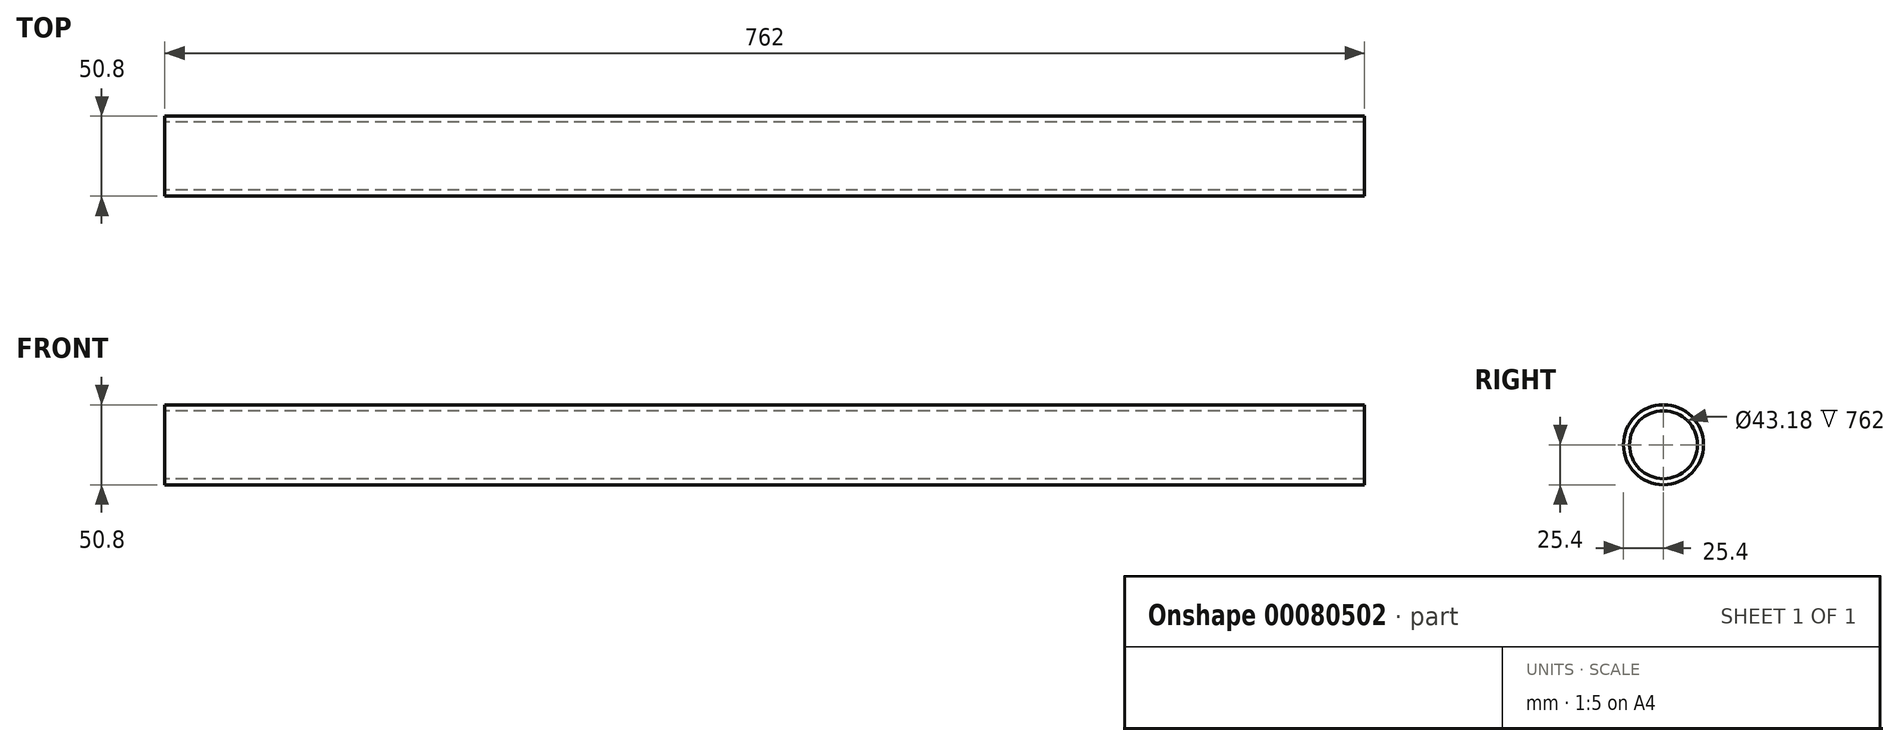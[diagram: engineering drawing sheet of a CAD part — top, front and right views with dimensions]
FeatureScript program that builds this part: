
annotation { "Feature Type Name" : "Feature", "Feature Type Description" : "" }
export const myFeature = defineFeature(function(context is Context, id is Id, definition is map)
    precondition{}
    {
        {
            var Q0;
            Q0=qCreatedBy(makeId("Right.planeOp"),FACE);
            var sketch = newSketch(context, id + "F0", { "sketchPlane" : qUnion([Q0])});
            skCircle(sketch, "E0", {"center": v(0, 0) * mm, "radius": 25.4 * mm});
            skCircle(sketch, "E1", {"center": v(0, 0) * mm, "radius": 21.59 * mm});
            skSolve(sketch);
        }
        {
            var Q0;
            Q0=makeQuery(id+"F0.imprint","IMPRINT",FACE,{"disambiguationData":[TD([[makeQuery(id+"F0.imprint","IMPRINT",EDGE,{"derivedFrom":sQuery(id+"F0.wireOp",EDGE,"E0")}),1.0]])]});
            extrude(context, id + "F1", {"entities" : qUnion([Q0]), "depth" : 762 * mm});
        }
    });
